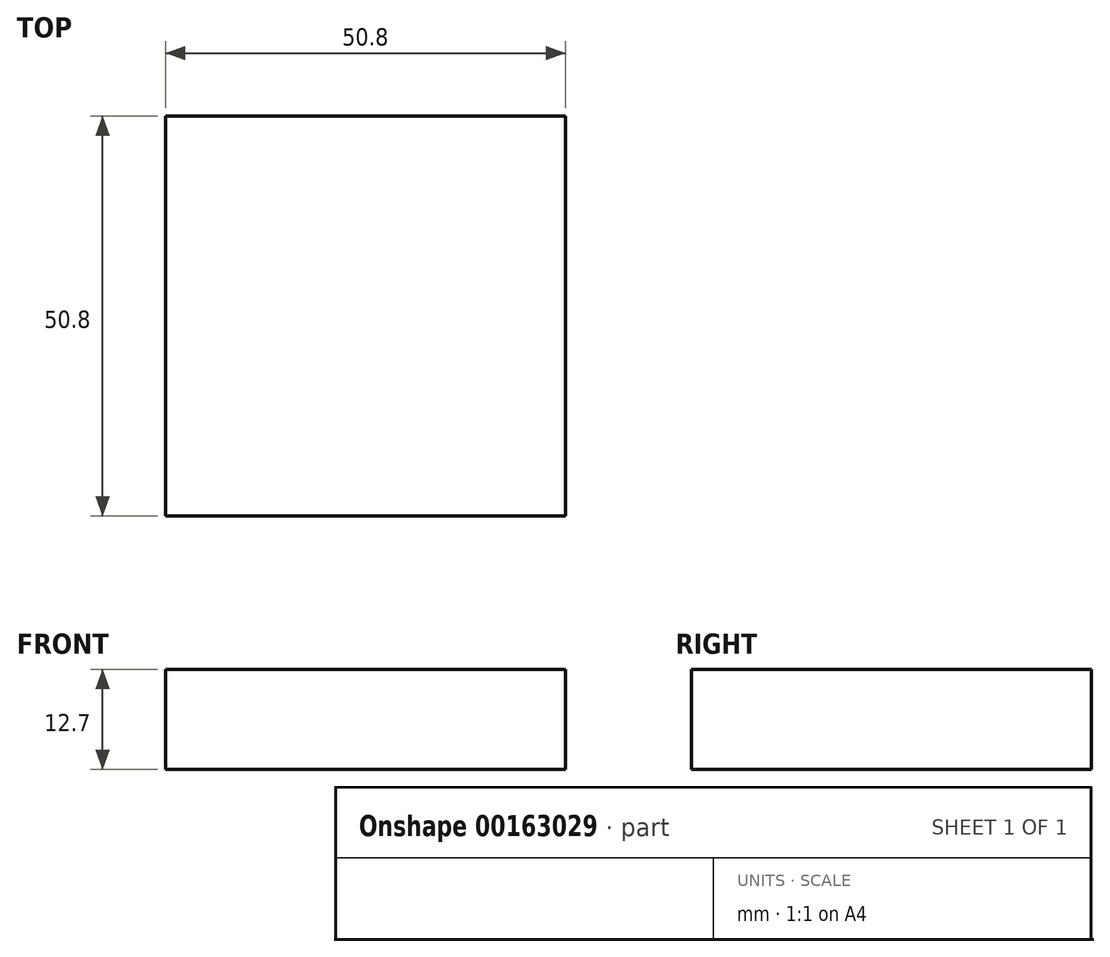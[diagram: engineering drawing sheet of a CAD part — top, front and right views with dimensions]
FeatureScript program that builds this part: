
annotation { "Feature Type Name" : "Feature", "Feature Type Description" : "" }
export const myFeature = defineFeature(function(context is Context, id is Id, definition is map)
    precondition{}
    {
        {
            var Q0;
            Q0=qCreatedBy(makeId("Front.planeOp"),FACE);
            var sketch = newSketch(context, id + "F0", { "sketchPlane" : qUnion([Q0])});
            skLineSegment(sketch, "E0.bottom", {"start": v(-25.4, 6.35) * mm, "end": v(25.4, 6.35) * mm});
            skLineSegment(sketch, "E0.top", {"start": v(-25.4, -6.35) * mm, "end": v(25.4, -6.35) * mm});
            skLineSegment(sketch, "E0.left", {"start": v(-25.4, 6.35) * mm, "end": v(-25.4, -6.35) * mm});
            skLineSegment(sketch, "E0.right", {"start": v(25.4, 6.35) * mm, "end": v(25.4, -6.35) * mm});
            skPoint(sketch, "E0.middle", {"position": v(0, 0) * mm});
            skSolve(sketch);
        }
        {
            var Q0;
            Q0 = qSketchRegion(id + "F0", true);
            extrude(context, id + "F1", {"entities" : qUnion([Q0]), "endBound" : BoundingType.SYMMETRIC, "depth" : 50.8 * mm});
        }
    });
